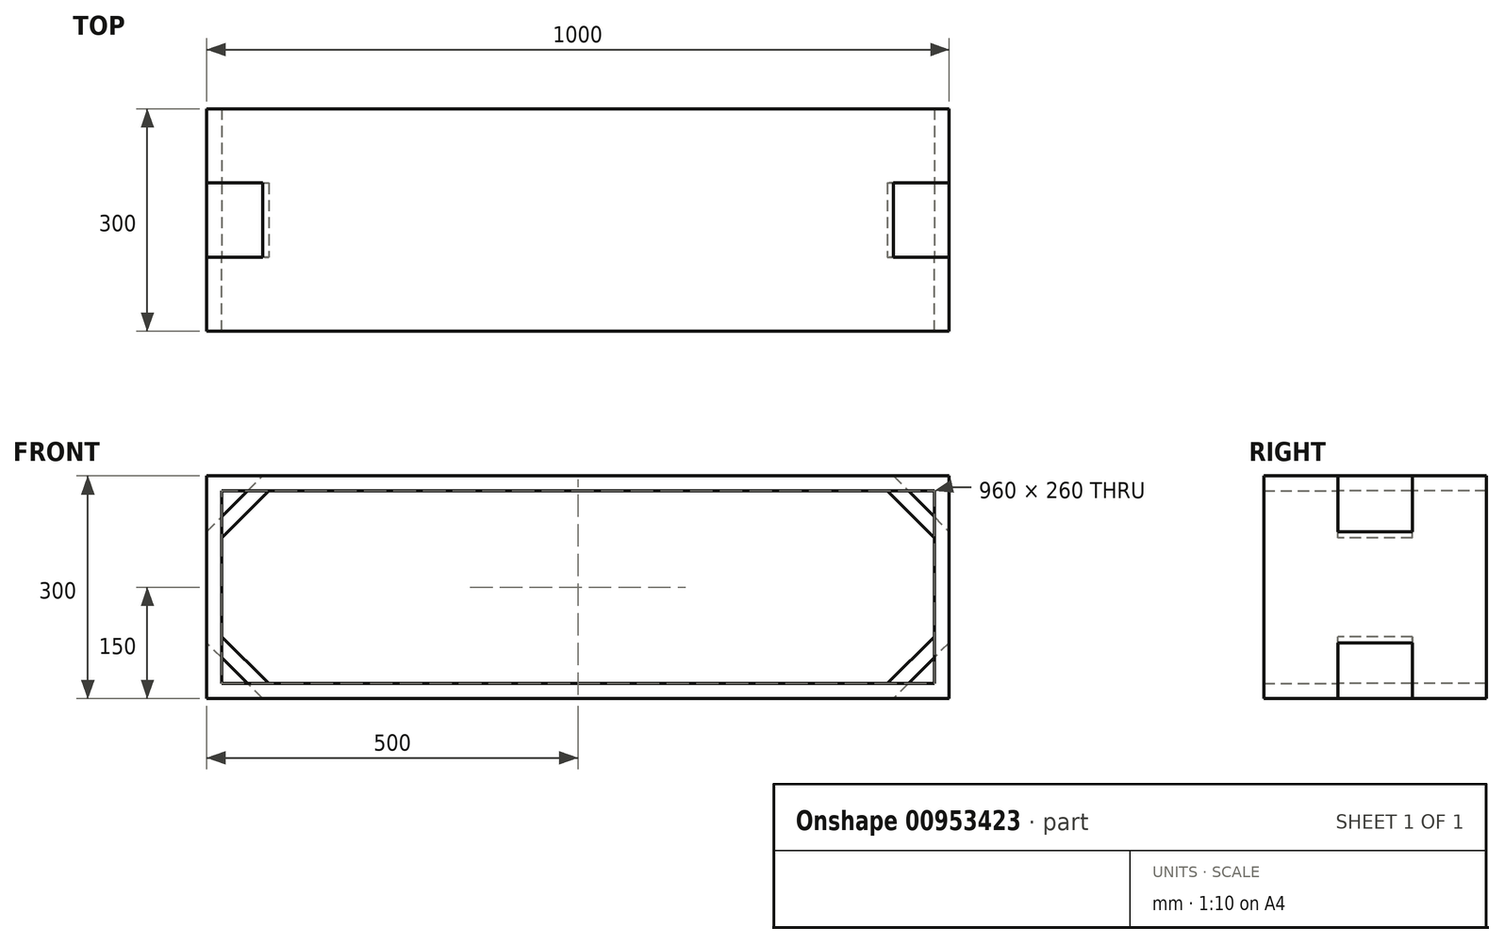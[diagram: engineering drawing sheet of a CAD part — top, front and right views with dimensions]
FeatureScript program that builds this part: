
annotation { "Feature Type Name" : "Feature", "Feature Type Description" : "" }
export const myFeature = defineFeature(function(context is Context, id is Id, definition is map)
    precondition{}
    {
        {
            var Q0;
            Q0=qCreatedBy(makeId("Front.planeOp"),FACE);
            var sketch = newSketch(context, id + "F0", { "sketchPlane" : qUnion([Q0])});
            skLineSegment(sketch, "E0.bottom", {"start": v(0, 0) * mm, "end": v(1000, 0) * mm});
            skLineSegment(sketch, "E0.top", {"start": v(0, 300) * mm, "end": v(1000, 300) * mm});
            skLineSegment(sketch, "E0.left", {"start": v(0, 0) * mm, "end": v(0, 300) * mm});
            skLineSegment(sketch, "E0.right", {"start": v(1000, 0) * mm, "end": v(1000, 300) * mm});
            skLineSegment(sketch, "E1.bottom", {"start": v(20, 20) * mm, "end": v(980, 20) * mm});
            skLineSegment(sketch, "E1.top", {"start": v(20, 280) * mm, "end": v(980, 280) * mm});
            skLineSegment(sketch, "E1.left", {"start": v(20, 20) * mm, "end": v(20, 280) * mm});
            skLineSegment(sketch, "E1.right", {"start": v(980, 20) * mm, "end": v(980, 280) * mm});
            skSolve(sketch);
        }
        {
            var Q0;
            Q0 = qSketchRegion(id + "F0", true);
            extrude(context, id + "F1", {"entities" : qUnion([Q0]), "depth" : 100 * mm, "offsetDistance" : 25 * mm});
        }
        {
            var Q0;
            Q0=qCreatedBy(makeId("Front.planeOp"),FACE);
            var sketch = newSketch(context, id + "F2", { "sketchPlane" : qUnion([Q0])});
            skLineSegment(sketch, "E2", {"start": v(0, 75) * mm, "end": v(0, 225) * mm});
            skLineSegment(sketch, "E3", {"start": v(0, 225) * mm, "end": v(75, 300) * mm});
            skLineSegment(sketch, "E4", {"start": v(75, 300) * mm, "end": v(925, 300) * mm});
            skLineSegment(sketch, "E5", {"start": v(925, 300) * mm, "end": v(1000, 225) * mm});
            skLineSegment(sketch, "E6", {"start": v(1000, 225) * mm, "end": v(1000, 75) * mm});
            skLineSegment(sketch, "E7", {"start": v(1000, 75) * mm, "end": v(925, 0) * mm});
            skLineSegment(sketch, "E8", {"start": v(925, 0) * mm, "end": v(75, 0) * mm});
            skLineSegment(sketch, "E9", {"start": v(75, 0) * mm, "end": v(0, 75) * mm});
            skLineSegment(sketch, "E10", {"start": v(20, 216.72) * mm, "end": v(83.28, 280) * mm});
            skLineSegment(sketch, "E11", {"start": v(83.28, 280) * mm, "end": v(916.72, 280) * mm});
            skLineSegment(sketch, "E12", {"start": v(916.72, 280) * mm, "end": v(980, 216.72) * mm});
            skLineSegment(sketch, "E13", {"start": v(980, 216.72) * mm, "end": v(980, 83.28) * mm});
            skLineSegment(sketch, "E14", {"start": v(980, 83.28) * mm, "end": v(916.72, 20) * mm});
            skLineSegment(sketch, "E15", {"start": v(916.72, 20) * mm, "end": v(83.28, 20) * mm});
            skLineSegment(sketch, "E16", {"start": v(83.28, 20) * mm, "end": v(20, 83.28) * mm});
            skLineSegment(sketch, "E17", {"start": v(20, 83.28) * mm, "end": v(20, 216.72) * mm});
            skSolve(sketch);
        }
        {
            var Q0;
            Q0 = qSketchRegion(id + "F2", true);
            extrude(context, id + "F3", {"entities" : qUnion([Q0]), "operationType" : NewBodyOperationType.ADD, "oppositeDirection" : true, "depth" : 100 * mm, "offsetDistance" : 25 * mm});
        }
        {
            var Q0;
            Q0=makeQuery(id+"F3.opExtrude","CAP_FACE",FACE,{"disambiguationData":[OSD([sQuery(id+"F2.wireOp",EDGE,"E2"),sQuery(id+"F2.wireOp",EDGE,"E3"),sQuery(id+"F2.wireOp",EDGE,"E4"),sQuery(id+"F2.wireOp",EDGE,"E5"),sQuery(id+"F2.wireOp",EDGE,"E6"),sQuery(id+"F2.wireOp",EDGE,"E7"),sQuery(id+"F2.wireOp",EDGE,"E8"),sQuery(id+"F2.wireOp",EDGE,"E9"),sQuery(id+"F2.wireOp",EDGE,"E10"),sQuery(id+"F2.wireOp",EDGE,"E11"),sQuery(id+"F2.wireOp",EDGE,"E12"),sQuery(id+"F2.wireOp",EDGE,"E13"),sQuery(id+"F2.wireOp",EDGE,"E14"),sQuery(id+"F2.wireOp",EDGE,"E15"),sQuery(id+"F2.wireOp",EDGE,"E16"),sQuery(id+"F2.wireOp",EDGE,"E17")])],"isStart":false});
            var sketch = newSketch(context, id + "F4", { "sketchPlane" : qUnion([Q0])});
            skLineSegment(sketch, "E18.bottom", {"start": v(0, 0) * mm, "end": v(-1000, 0) * mm});
            skLineSegment(sketch, "E18.top", {"start": v(0, 300) * mm, "end": v(-1000, 300) * mm});
            skLineSegment(sketch, "E18.left", {"start": v(0, 0) * mm, "end": v(0, 300) * mm});
            skLineSegment(sketch, "E18.right", {"start": v(-1000, 0) * mm, "end": v(-1000, 300) * mm});
            skLineSegment(sketch, "E19.bottom", {"start": v(-20, 20) * mm, "end": v(-980, 20) * mm});
            skLineSegment(sketch, "E19.top", {"start": v(-20, 280) * mm, "end": v(-980, 280) * mm});
            skLineSegment(sketch, "E19.left", {"start": v(-20, 20) * mm, "end": v(-20, 280) * mm});
            skLineSegment(sketch, "E19.right", {"start": v(-980, 20) * mm, "end": v(-980, 280) * mm});
            skSolve(sketch);
        }
        {
            var Q0;
            Q0 = qSketchRegion(id + "F4", true);
            extrude(context, id + "F5", {"entities" : qUnion([Q0]), "operationType" : NewBodyOperationType.ADD, "depth" : 100 * mm, "offsetDistance" : 25 * mm});
        }
    });
